# Revit family: blp150e75ns_PC_HW
name_source: partatom
category: Mechanical Equipment
units: mm (PartAtom-declared; Revit-internal decimal feet)

## family parameters
Always vertical = Yes
Classification = None
Cut with Voids When Loaded = No
Maintain Annotation Orientation = No
OmniClass Number = 23.75.70.00
OmniClass Title = HVAC Distribution Devices
Part Type = Normal
Room Calculation Point = No
Round Connector Dimension = Use Diameter
Shared = No
Work Plane-Based = No

## types (1)
- Standard
    Area = 37.23 SF
    Center of Gravity = X: -0.017 in Y: 5.123 in Z: 2.320 in
    Connector_1_Diameter = 0' - 5 27/32"
    Connector_2_Diameter = 0' - 5 21/32"
    Connector_3_Diameter = 0' - 5 27/32"
    Connector_4_Diameter = 0' - 5 25/32"
    Default Elevation = 0' - 0"
    Density = 62.43 lb/ft³
    Design State = 1
    Manufacturer = Broan Nutone Venmar
    Mass = 4.03 lbm
    Model = BLP150E75NS
    Part Number = blp150e75ns_PC_HW
    Preprocessor = CREO PARAMETRIC BY PTC INC, 2023424
    Requested Accuracy = Low
    Revision Number = 1LAST_VERSION
    Sending System = CREO PARAMETRIC BY PTC INC, 2023424
    Title = BLP150E75NS_ASM
    Volume = 0.06 CF

## geometry (parser evidence)
native form markers: Sweep x2
no freeform markers — native parametric forms only
